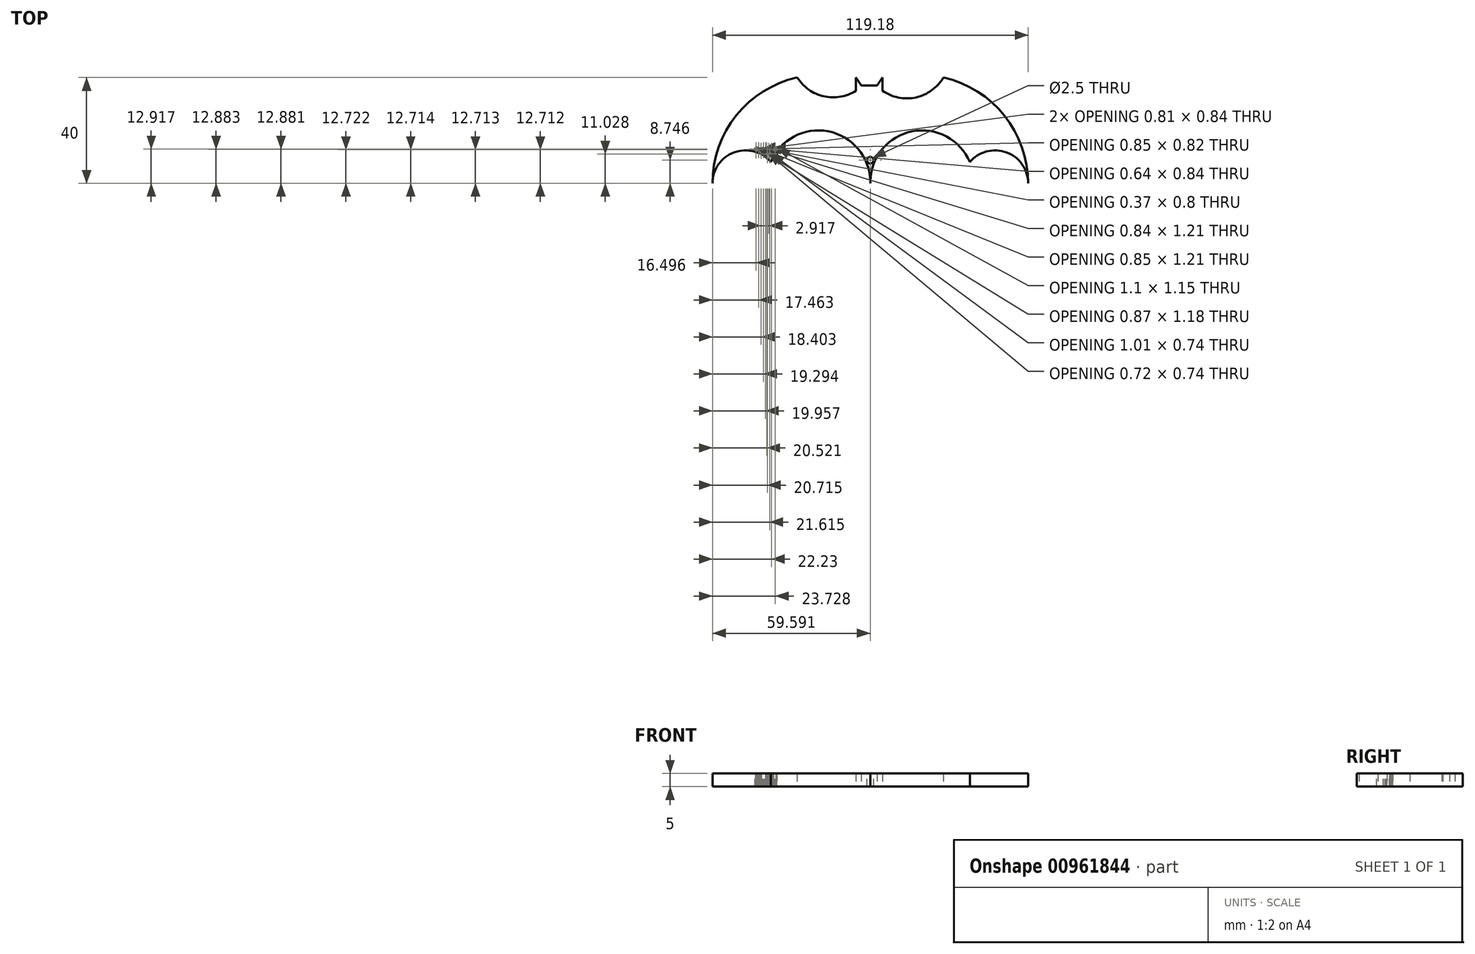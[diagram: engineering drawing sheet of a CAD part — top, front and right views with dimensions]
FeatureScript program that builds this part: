
annotation { "Feature Type Name" : "Feature", "Feature Type Description" : "" }
export const myFeature = defineFeature(function(context is Context, id is Id, definition is map)
    precondition{}
    {
        {
            var Q0;
            Q0=qCreatedBy(makeId("Top.planeOp"),FACE);
            var sketch = newSketch(context, id + "F0", { "sketchPlane" : qUnion([Q0])});
            skArc(sketch, "E0", {"start": v(58.2, -8) * mm, "mid": v(50, 3.7) * mm, "end": v(36.2, 0) * mm});
            skArc(sketch, "E1", {"start": v(-39, 0) * mm, "mid": v(-52.8, 3.7) * mm, "end": v(-61, -8) * mm});
            skArc(sketch, "E2", {"start": v(-1.4, -8) * mm, "mid": v(-16.88, 11.57) * mm, "end": v(-39, 0) * mm});
            skArc(sketch, "E3", {"start": v(36.2, 0) * mm, "mid": v(14.08, 11.57) * mm, "end": v(-1.4, -8) * mm});
            skLineSegment(sketch, "E4", {"start": v(-4.8, 29) * mm, "end": v(-6.8, 32) * mm});
            skLineSegment(sketch, "E5", {"start": v(1.2, 29) * mm, "end": v(3.2, 32) * mm});
            skLineSegment(sketch, "E6", {"start": v(-4.8, 29) * mm, "end": v(1.2, 29) * mm});
            skPoint(sketch, "E7", {"position": v(-29, 32) * mm});
            skArc(sketch, "E8", {"start": v(-29, 32) * mm, "mid": v(-52, 17.61) * mm, "end": v(-61, -8) * mm});
            skArc(sketch, "E9", {"start": v(58.2, -8) * mm, "mid": v(49.2, 17.61) * mm, "end": v(26.2, 32) * mm});
            skLineSegment(sketch, "E10", {"start": v(-6.8, 32) * mm, "end": v(-6.8, 27) * mm});
            skLineSegment(sketch, "E11", {"start": v(3.2, 32) * mm, "end": v(3.2, 27) * mm});
            skArc(sketch, "E12", {"start": v(-29, 32) * mm, "mid": v(-18.94, 24.87) * mm, "end": v(-6.8, 27) * mm});
            skArc(sketch, "E13", {"start": v(3.2, 27) * mm, "mid": v(15.8, 24.46) * mm, "end": v(26.2, 32) * mm});
            skSolve(sketch);
        }
        {
            var Q0;
            Q0=qSketchRegion(id+"F0",true);
            extrude(context, id + "F1", {"entities" : qUnion([Q0]), "depth" : 5 * mm, "offsetDistance" : 25 * mm});
        }
        {
            var Q0;
            Q0=makeQuery(id+"F1.opExtrude","CAP_FACE",FACE,{"disambiguationData":[OSD([sQuery(id+"F0.wireOp",EDGE,"E0"),sQuery(id+"F0.wireOp",EDGE,"E1"),sQuery(id+"F0.wireOp",EDGE,"E2"),sQuery(id+"F0.wireOp",EDGE,"E3"),sQuery(id+"F0.wireOp",EDGE,"E4"),sQuery(id+"F0.wireOp",EDGE,"E5"),sQuery(id+"F0.wireOp",EDGE,"E6"),sQuery(id+"F0.wireOp",EDGE,"E8"),sQuery(id+"F0.wireOp",EDGE,"E9"),sQuery(id+"F0.wireOp",EDGE,"E10"),sQuery(id+"F0.wireOp",EDGE,"E11"),sQuery(id+"F0.wireOp",EDGE,"E12"),sQuery(id+"F0.wireOp",EDGE,"E13")])],"isStart":false});
            var sketch = newSketch(context, id + "F2", { "sketchPlane" : qUnion([Q0])});
            skText(sketch, "E14", { "text": "Shakisan.R", "fontName": "Tinos-BoldItalic.ttf"});
            const initialGuessF2  = {"E14": [-0.04496, 0.00431, 1, 0, 0.00126]};
            skSetInitialGuess(sketch, initialGuessF2);
            skSolve(sketch);
        }
        {
            var Q0;
            Q0=qSketchRegion(id+"F2",true);
            extrude(context, id + "F3", {"entities" : qUnion([Q0]), "operationType" : NewBodyOperationType.REMOVE, "oppositeDirection" : true, "depth" : 25 * mm, "offsetDistance" : 25 * mm});
        }
        {
            var Q0;
            {var subQ0=sQuery(id+"F0.wireOp",EDGE,"E10");var subQ1=sQuery(id+"F0.wireOp",EDGE,"E8");var subQ2=sQuery(id+"F0.wireOp",EDGE,"E6");var subQ3=sQuery(id+"F0.wireOp",EDGE,"E4");var subQ4=sQuery(id+"F0.wireOp",EDGE,"E5");var subQ5=sQuery(id+"F0.wireOp",EDGE,"E0");var subQ6=sQuery(id+"F0.wireOp",EDGE,"E9");var subQ7=sQuery(id+"F0.wireOp",EDGE,"E1");var subQ8=sQuery(id+"F0.wireOp",EDGE,"E3");var subQ9=sQuery(id+"F0.wireOp",EDGE,"E2");var subQ11=sQuery(id+"F0.wireOp",EDGE,"E11");var subQ12=sQuery(id+"F0.wireOp",EDGE,"E12");var subQ13=sQuery(id+"F0.wireOp",EDGE,"E13");Q0=makeQuery(id+"F3.boolean.opBoolean","SPLIT",FACE,{"disambiguationData":[TD([makeQuery(id+"F1.opExtrude","SWEPT_FACE",FACE,{"disambiguationData":[OSD([subQ5])]})])],"derivedFrom":makeQuery(id+"F1.opExtrude","CAP_FACE",FACE,{"disambiguationData":[OSD([subQ5,subQ7,subQ9,subQ8,subQ3,subQ4,subQ2,subQ1,subQ6,subQ0,subQ11,subQ12,subQ13])],"isStart":false})});}
            var sketch = newSketch(context, id + "F4", { "sketchPlane" : qUnion([Q0])});
            skText(sketch, "E15", { "text": "TM", "fontName": "Tinos-Bold.ttf"});
            const initialGuessF4  = {"E15": [-0.04065, 0.00266, 1, 0, 0.00081]};
            skSetInitialGuess(sketch, initialGuessF4);
            skSolve(sketch);
        }
        {
            var Q0;
            Q0=qSketchRegion(id+"F4",true);
            extrude(context, id + "F5", {"entities" : qUnion([Q0]), "operationType" : NewBodyOperationType.REMOVE, "oppositeDirection" : true, "depth" : 25 * mm, "offsetDistance" : 25 * mm});
        }
        {
            var Q0;
            {var subQ0=sQuery(id+"F0.wireOp",EDGE,"E10");var subQ1=sQuery(id+"F0.wireOp",EDGE,"E8");var subQ2=sQuery(id+"F0.wireOp",EDGE,"E6");var subQ3=sQuery(id+"F0.wireOp",EDGE,"E4");var subQ4=sQuery(id+"F0.wireOp",EDGE,"E5");var subQ5=sQuery(id+"F0.wireOp",EDGE,"E0");var subQ6=sQuery(id+"F0.wireOp",EDGE,"E9");var subQ7=sQuery(id+"F0.wireOp",EDGE,"E1");var subQ8=sQuery(id+"F0.wireOp",EDGE,"E3");var subQ9=sQuery(id+"F0.wireOp",EDGE,"E2");var subQ11=sQuery(id+"F0.wireOp",EDGE,"E11");var subQ12=sQuery(id+"F0.wireOp",EDGE,"E12");var subQ13=sQuery(id+"F0.wireOp",EDGE,"E13");Q0=makeQuery(id+"F3.boolean.opBoolean","SPLIT",FACE,{"disambiguationData":[TD([makeQuery(id+"F1.opExtrude","SWEPT_FACE",FACE,{"disambiguationData":[OSD([subQ5])]})])],"derivedFrom":makeQuery(id+"F1.opExtrude","CAP_FACE",FACE,{"disambiguationData":[OSD([subQ5,subQ7,subQ9,subQ8,subQ3,subQ4,subQ2,subQ1,subQ6,subQ0,subQ11,subQ12,subQ13])],"isStart":false})});}
            var sketch = newSketch(context, id + "F6", { "sketchPlane" : qUnion([Q0])});
            skCircle(sketch, "E16", {"center": v(-1.4, 0.75) * mm, "radius": 1.25 * mm});
            skPoint(sketch, "E17.start.orphan", {"position": v(-3.24, 0.75) * mm});
            skPoint(sketch, "E18.trimOffspring.end.orphan", {"position": v(0.45, 0.75) * mm});
            skSolve(sketch);
        }
        {
            var Q0;
            Q0=makeQuery(id+"F6.imprint","IMPRINT",FACE,{"disambiguationData":[TD([[makeQuery(id+"F6.imprint","IMPRINT",EDGE,{"derivedFrom":sQuery(id+"F6.wireOp",EDGE,"E16")}),1.0]])]});
            extrude(context, id + "F7", {"entities" : qUnion([Q0]), "operationType" : NewBodyOperationType.REMOVE, "oppositeDirection" : true, "depth" : 25 * mm, "offsetDistance" : 25 * mm});
        }
    });
